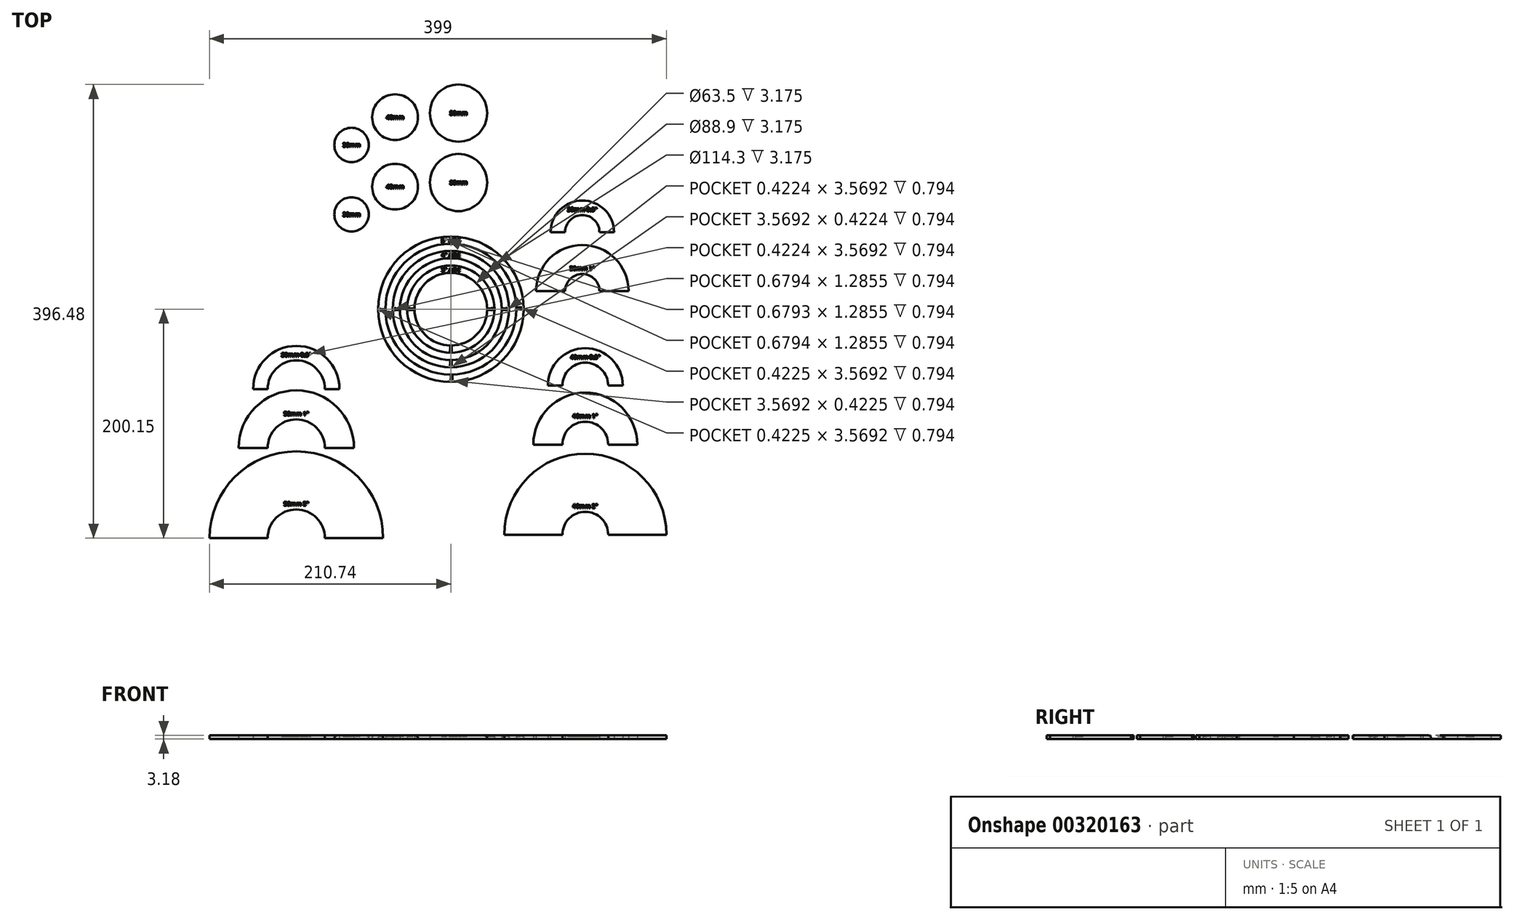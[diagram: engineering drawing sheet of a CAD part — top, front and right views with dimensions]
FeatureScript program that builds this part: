
annotation { "Feature Type Name" : "Feature", "Feature Type Description" : "" }
export const myFeature = defineFeature(function(context is Context, id is Id, definition is map)
    precondition{}
    {
        {
            var Q0;
            Q0=qCreatedBy(makeId("Top.planeOp"),FACE);
            var sketch = newSketch(context, id + "F0", { "sketchPlane" : qUnion([Q0])});
            skCircle(sketch, "E0", {"center": v(0, 0) * mm, "radius": 38.1 * mm});
            skCircle(sketch, "E1", {"center": v(0, 0) * mm, "radius": 31.75 * mm});
            skCircle(sketch, "E2", {"center": v(0, 0) * mm, "radius": 50.8 * mm});
            skCircle(sketch, "E3", {"center": v(0, 0) * mm, "radius": 44.45 * mm});
            skCircle(sketch, "E4", {"center": v(114.85, 67.2) * mm, "radius": 27.7 * mm});
            skCircle(sketch, "E5", {"center": v(114.85, 67.2) * mm, "radius": 15 * mm});
            skCircle(sketch, "E6", {"center": v(114.85, 67.2) * mm, "radius": 40.4 * mm});
            skCircle(sketch, "E7", {"center": v(117.46, -66.84) * mm, "radius": 32.7 * mm});
            skCircle(sketch, "E8", {"center": v(117.46, -66.84) * mm, "radius": 20 * mm});
            skCircle(sketch, "E9", {"center": v(117.46, -66.84) * mm, "radius": 45.4 * mm});
            skCircle(sketch, "E10", {"center": v(117.46, -66.84) * mm, "radius": 70.8 * mm});
            skLineSegment(sketch, "E11", {"start": v(74.45, 67.2) * mm, "end": v(87.15, 67.2) * mm});
            skLineSegment(sketch, "E12", {"start": v(87.15, 67.2) * mm, "end": v(99.85, 67.2) * mm});
            skLineSegment(sketch, "E13", {"start": v(99.85, 67.2) * mm, "end": v(114.85, 67.2) * mm});
            skLineSegment(sketch, "E14", {"start": v(129.85, 67.2) * mm, "end": v(114.85, 67.2) * mm});
            skLineSegment(sketch, "E15", {"start": v(129.85, 67.2) * mm, "end": v(142.55, 67.2) * mm});
            skLineSegment(sketch, "E16", {"start": v(142.55, 67.2) * mm, "end": v(155.25, 67.2) * mm});
            skLineSegment(sketch, "E17", {"start": v(117.46, -66.84) * mm, "end": v(97.46, -66.84) * mm});
            skLineSegment(sketch, "E18", {"start": v(97.46, -66.84) * mm, "end": v(84.76, -66.84) * mm});
            skLineSegment(sketch, "E19", {"start": v(84.76, -66.84) * mm, "end": v(72.06, -66.84) * mm});
            skLineSegment(sketch, "E20", {"start": v(72.06, -66.84) * mm, "end": v(46.66, -66.84) * mm});
            skLineSegment(sketch, "E21", {"start": v(117.46, -66.84) * mm, "end": v(137.46, -66.84) * mm});
            skLineSegment(sketch, "E22", {"start": v(137.46, -66.84) * mm, "end": v(150.16, -66.84) * mm});
            skLineSegment(sketch, "E23", {"start": v(150.16, -66.84) * mm, "end": v(162.86, -66.84) * mm});
            skLineSegment(sketch, "E24", {"start": v(162.86, -66.84) * mm, "end": v(188.26, -66.84) * mm});
            skCircle(sketch, "E25", {"center": v(-134.94, -69.85) * mm, "radius": 37.7 * mm});
            skCircle(sketch, "E26", {"center": v(-134.94, -69.85) * mm, "radius": 25 * mm});
            skCircle(sketch, "E27", {"center": v(-134.94, -69.85) * mm, "radius": 50.4 * mm});
            skCircle(sketch, "E28", {"center": v(-134.94, -69.85) * mm, "radius": 75.8 * mm});
            skLineSegment(sketch, "E29", {"start": v(-134.94, -69.85) * mm, "end": v(-159.94, -69.85) * mm});
            skLineSegment(sketch, "E30", {"start": v(-159.94, -69.85) * mm, "end": v(-172.64, -69.85) * mm});
            skLineSegment(sketch, "E31", {"start": v(-172.64, -69.85) * mm, "end": v(-185.34, -69.85) * mm});
            skLineSegment(sketch, "E32", {"start": v(-185.34, -69.85) * mm, "end": v(-210.74, -69.85) * mm});
            skLineSegment(sketch, "E33", {"start": v(-134.94, -69.85) * mm, "end": v(-109.94, -69.85) * mm});
            skLineSegment(sketch, "E34", {"start": v(-109.94, -69.85) * mm, "end": v(-97.24, -69.85) * mm});
            skLineSegment(sketch, "E35", {"start": v(-97.24, -69.85) * mm, "end": v(-84.54, -69.85) * mm});
            skLineSegment(sketch, "E36", {"start": v(-84.54, -69.85) * mm, "end": v(-59.14, -69.85) * mm});
            skCircle(sketch, "E37", {"center": v(0, 0) * mm, "radius": 57.15 * mm});
            skCircle(sketch, "E38", {"center": v(0, 0) * mm, "radius": 63.5 * mm});
            skCircle(sketch, "E39", {"center": v(-86.71, 82.78) * mm, "radius": 15 * mm});
            skCircle(sketch, "E40", {"center": v(-48.67, 107.05) * mm, "radius": 20 * mm});
            skCircle(sketch, "E41", {"center": v(6.75, 110.62) * mm, "radius": 25 * mm});
            skSolve(sketch);
        }
        {
            var Q0;
            Q0=makeQuery(id+"F0.imprint","IMPRINT",FACE,{"disambiguationData":[TD([[makeQuery(id+"F0.imprint","IMPRINT",EDGE,{"derivedFrom":sQuery(id+"F0.wireOp",EDGE,"E0")}),1.0]])]});
            var Q1;
            Q1=makeQuery(id+"F0.imprint","IMPRINT",FACE,{"disambiguationData":[TD([[makeQuery(id+"F0.imprint","IMPRINT",EDGE,{"derivedFrom":sQuery(id+"F0.wireOp",EDGE,"E2")}),1.0]])]});
            var Q2;
            {var subQ0=sQuery(id+"F0.wireOp",EDGE,"E12");Q2=makeQuery(id+"F0.imprint","IMPRINT",FACE,{"disambiguationData":[TD([[makeQuery(id+"F0.imprint","IMPRINT",EDGE,{"derivedFrom":subQ0}),1.0]])]});}
            var Q3;
            {var subQ0=sQuery(id+"F0.wireOp",EDGE,"E18");Q3=makeQuery(id+"F0.imprint","IMPRINT",FACE,{"disambiguationData":[TD([[makeQuery(id+"F0.imprint","IMPRINT",EDGE,{"derivedFrom":subQ0}),-1.0]])]});}
            var Q4;
            {var subQ0=sQuery(id+"F0.wireOp",EDGE,"E30");Q4=makeQuery(id+"F0.imprint","IMPRINT",FACE,{"disambiguationData":[TD([[makeQuery(id+"F0.imprint","IMPRINT",EDGE,{"derivedFrom":subQ0}),-1.0]])]});}
            var Q5;
            Q5=makeQuery(id+"F0.imprint","IMPRINT",FACE,{"disambiguationData":[TD([[makeQuery(id+"F0.imprint","IMPRINT",EDGE,{"derivedFrom":sQuery(id+"F0.wireOp",EDGE,"E37")}),-1.0]])]});
            var Q6;
            Q6=makeQuery(id+"F0.imprint","IMPRINT",FACE,{"disambiguationData":[TD([[makeQuery(id+"F0.imprint","IMPRINT",EDGE,{"derivedFrom":sQuery(id+"F0.wireOp",EDGE,"E41")}),1.0]])]});
            var Q7;
            Q7=makeQuery(id+"F0.imprint","IMPRINT",FACE,{"disambiguationData":[TD([[makeQuery(id+"F0.imprint","IMPRINT",EDGE,{"derivedFrom":sQuery(id+"F0.wireOp",EDGE,"E40")}),1.0]])]});
            var Q8;
            Q8=makeQuery(id+"F0.imprint","IMPRINT",FACE,{"disambiguationData":[TD([[makeQuery(id+"F0.imprint","IMPRINT",EDGE,{"derivedFrom":sQuery(id+"F0.wireOp",EDGE,"E39")}),1.0]])]});
            extrude(context, id + "F1", {"entities" : qUnion([Q0, Q1, Q2, Q3, Q4, Q5, Q6, Q7, Q8]), "depth" : 3.17 * mm});
        }
        {
            var Q0;
            {var subQ0=sQuery(id+"F0.wireOp",EDGE,"E30");Q0=makeQuery(id+"F0.imprint","IMPRINT",FACE,{"disambiguationData":[TD([[makeQuery(id+"F0.imprint","IMPRINT",EDGE,{"derivedFrom":subQ0}),-1.0]])]});}
            var Q1;
            {var subQ0=sQuery(id+"F0.wireOp",EDGE,"E31");Q1=makeQuery(id+"F0.imprint","IMPRINT",FACE,{"disambiguationData":[TD([[makeQuery(id+"F0.imprint","IMPRINT",EDGE,{"derivedFrom":subQ0}),-1.0]])]});}
            var Q2;
            {var subQ0=sQuery(id+"F0.wireOp",EDGE,"E18");Q2=makeQuery(id+"F0.imprint","IMPRINT",FACE,{"disambiguationData":[TD([[makeQuery(id+"F0.imprint","IMPRINT",EDGE,{"derivedFrom":subQ0}),-1.0]])]});}
            var Q3;
            {var subQ0=sQuery(id+"F0.wireOp",EDGE,"E19");Q3=makeQuery(id+"F0.imprint","IMPRINT",FACE,{"disambiguationData":[TD([[makeQuery(id+"F0.imprint","IMPRINT",EDGE,{"derivedFrom":subQ0}),-1.0]])]});}
            var Q4;
            {var subQ0=sQuery(id+"F0.wireOp",EDGE,"E12");Q4=makeQuery(id+"F0.imprint","IMPRINT",FACE,{"disambiguationData":[TD([[makeQuery(id+"F0.imprint","IMPRINT",EDGE,{"derivedFrom":subQ0}),1.0]])]});}
            var Q5;
            {var subQ0=sQuery(id+"F0.wireOp",EDGE,"E11");Q5=makeQuery(id+"F0.imprint","IMPRINT",FACE,{"disambiguationData":[TD([[makeQuery(id+"F0.imprint","IMPRINT",EDGE,{"derivedFrom":subQ0}),1.0]])]});}
            extrude(context, id + "F2", {"entities" : qUnion([Q0, Q1, Q2, Q3, Q4, Q5]), "depth" : 3.17 * mm});
        }
        {
            var Q0;
            {var subQ0=sQuery(id+"F0.wireOp",EDGE,"E18");Q0=makeQuery(id+"F0.imprint","IMPRINT",FACE,{"disambiguationData":[TD([[makeQuery(id+"F0.imprint","IMPRINT",EDGE,{"derivedFrom":subQ0}),-1.0]])]});}
            var Q1;
            {var subQ0=sQuery(id+"F0.wireOp",EDGE,"E19");Q1=makeQuery(id+"F0.imprint","IMPRINT",FACE,{"disambiguationData":[TD([[makeQuery(id+"F0.imprint","IMPRINT",EDGE,{"derivedFrom":subQ0}),-1.0]])]});}
            var Q2;
            {var subQ0=sQuery(id+"F0.wireOp",EDGE,"E20");Q2=makeQuery(id+"F0.imprint","IMPRINT",FACE,{"disambiguationData":[TD([[makeQuery(id+"F0.imprint","IMPRINT",EDGE,{"derivedFrom":subQ0}),-1.0]])]});}
            var Q3;
            {var subQ0=sQuery(id+"F0.wireOp",EDGE,"E30");Q3=makeQuery(id+"F0.imprint","IMPRINT",FACE,{"disambiguationData":[TD([[makeQuery(id+"F0.imprint","IMPRINT",EDGE,{"derivedFrom":subQ0}),-1.0]])]});}
            var Q4;
            {var subQ0=sQuery(id+"F0.wireOp",EDGE,"E31");Q4=makeQuery(id+"F0.imprint","IMPRINT",FACE,{"disambiguationData":[TD([[makeQuery(id+"F0.imprint","IMPRINT",EDGE,{"derivedFrom":subQ0}),-1.0]])]});}
            var Q5;
            {var subQ0=sQuery(id+"F0.wireOp",EDGE,"E32");Q5=makeQuery(id+"F0.imprint","IMPRINT",FACE,{"disambiguationData":[TD([[makeQuery(id+"F0.imprint","IMPRINT",EDGE,{"derivedFrom":subQ0}),-1.0]])]});}
            extrude(context, id + "F3", {"entities" : qUnion([Q0, Q1, Q2, Q3, Q4, Q5]), "depth" : 3.17 * mm});
        }
        {
            var Q0;
            Q0=makeQuery(id+"F2.opExtrude","SWEPT_BODY",BODY,{"disambiguationData":[OSD([sQuery(id+"F0.wireOp",EDGE,"E8"),sQuery(id+"F0.wireOp",EDGE,"E9"),sQuery(id+"F0.wireOp",EDGE,"E18"),sQuery(id+"F0.wireOp",EDGE,"E19"),sQuery(id+"F0.wireOp",EDGE,"E22"),sQuery(id+"F0.wireOp",EDGE,"E23")])]});
            var Q1;
            Q1=makeQuery(id+"F2.opExtrude","SWEPT_BODY",BODY,{"disambiguationData":[OSD([sQuery(id+"F0.wireOp",EDGE,"E26"),sQuery(id+"F0.wireOp",EDGE,"E27"),sQuery(id+"F0.wireOp",EDGE,"E30"),sQuery(id+"F0.wireOp",EDGE,"E31"),sQuery(id+"F0.wireOp",EDGE,"E34"),sQuery(id+"F0.wireOp",EDGE,"E35")])]});
            var Q2;
            Q2=makeQuery(id+"F2.opExtrude","SWEPT_BODY",BODY,{"disambiguationData":[OSD([sQuery(id+"F0.wireOp",EDGE,"E5"),sQuery(id+"F0.wireOp",EDGE,"E6"),sQuery(id+"F0.wireOp",EDGE,"E11"),sQuery(id+"F0.wireOp",EDGE,"E12"),sQuery(id+"F0.wireOp",EDGE,"E15"),sQuery(id+"F0.wireOp",EDGE,"E16")])]});
            transform(context, id + "F4", {"entities" : qUnion([Q0, Q1, Q2]), "transformType" : TransformType.TRANSLATION_3D, "dx" : 0 * mm, "dy" : -51.56 * mm, "dz" : 0 * mm, "makeCopy" : false});
        }
        {
            var Q0;
            Q0=makeQuery(id+"F3.opExtrude","SWEPT_BODY",BODY,{"disambiguationData":[OSD([sQuery(id+"F0.wireOp",EDGE,"E8"),sQuery(id+"F0.wireOp",EDGE,"E10"),sQuery(id+"F0.wireOp",EDGE,"E18"),sQuery(id+"F0.wireOp",EDGE,"E19"),sQuery(id+"F0.wireOp",EDGE,"E20"),sQuery(id+"F0.wireOp",EDGE,"E22"),sQuery(id+"F0.wireOp",EDGE,"E23"),sQuery(id+"F0.wireOp",EDGE,"E24")])]});
            var Q1;
            Q1=makeQuery(id+"F3.opExtrude","SWEPT_BODY",BODY,{"disambiguationData":[OSD([sQuery(id+"F0.wireOp",EDGE,"E26"),sQuery(id+"F0.wireOp",EDGE,"E28"),sQuery(id+"F0.wireOp",EDGE,"E30"),sQuery(id+"F0.wireOp",EDGE,"E31"),sQuery(id+"F0.wireOp",EDGE,"E32"),sQuery(id+"F0.wireOp",EDGE,"E34"),sQuery(id+"F0.wireOp",EDGE,"E35"),sQuery(id+"F0.wireOp",EDGE,"E36")])]});
            transform(context, id + "F5", {"entities" : qUnion([Q0, Q1]), "transformType" : TransformType.TRANSLATION_3D, "dx" : 0 * mm, "dy" : -130.3 * mm, "dz" : 0 * mm, "makeCopy" : false});
        }
        {
            var Q0;
            Q0=makeQuery(id+"F1.opExtrude","CAP_FACE",FACE,{"disambiguationData":[OSD([sQuery(id+"F0.wireOp",EDGE,"E2"),sQuery(id+"F0.wireOp",EDGE,"E3")])],"isStart":false});
            var sketch = newSketch(context, id + "F6", { "sketchPlane" : qUnion([Q0])});
            skText(sketch, "E42", { "text": "4\" AOE", "fontName": "OpenSans-Bold.ttf"});
            skText(sketch, "E43", { "text": "3\" AOE", "fontName": "OpenSans-Bold.ttf"});
            skText(sketch, "E44", { "text": "50mm 0.5\"", "fontName": "OpenSans-Bold.ttf"});
            skText(sketch, "E45", { "text": "50mm 1\"", "fontName": "OpenSans-Bold.ttf"});
            skText(sketch, "E46", { "text": "50mm 2\"", "fontName": "OpenSans-Bold.ttf"});
            skText(sketch, "E47", { "text": "30mm 0.5\"", "fontName": "OpenSans-Bold.ttf"});
            skArc(sketch, "E48.0.0", {"start": v(-159.94, -200.15) * mm, "mid": v(-134.94, -175.15) * mm, "end": v(-109.94, -200.15) * mm, "construction": true});
            skLineSegment(sketch, "E48.0.1", {"start": v(-109.94, -200.15) * mm, "end": v(-59.14, -200.15) * mm, "construction": true});
            skArc(sketch, "E48.0.2", {"start": v(-59.14, -200.15) * mm, "mid": v(-134.94, -124.35) * mm, "end": v(-210.74, -200.15) * mm, "construction": true});
            skLineSegment(sketch, "E48.0.3", {"start": v(-210.74, -200.15) * mm, "end": v(-159.94, -200.15) * mm, "construction": true});
            skArc(sketch, "E49.0.0", {"start": v(-159.94, -121.41) * mm, "mid": v(-134.94, -96.41) * mm, "end": v(-109.94, -121.41) * mm, "construction": true});
            skLineSegment(sketch, "E49.0.1", {"start": v(-109.94, -121.41) * mm, "end": v(-84.54, -121.41) * mm, "construction": true});
            skArc(sketch, "E49.0.2", {"start": v(-84.54, -121.41) * mm, "mid": v(-134.94, -71.01) * mm, "end": v(-185.34, -121.41) * mm, "construction": true});
            skLineSegment(sketch, "E49.0.3", {"start": v(-185.34, -121.41) * mm, "end": v(-159.94, -121.41) * mm, "construction": true});
            skArc(sketch, "E50.0.0", {"start": v(-159.94, -69.85) * mm, "mid": v(-134.94, -44.85) * mm, "end": v(-109.94, -69.85) * mm, "construction": true});
            skLineSegment(sketch, "E50.0.1", {"start": v(-109.94, -69.85) * mm, "end": v(-97.24, -69.85) * mm, "construction": true});
            skArc(sketch, "E50.0.2", {"start": v(-97.24, -69.85) * mm, "mid": v(-134.94, -32.15) * mm, "end": v(-172.64, -69.85) * mm, "construction": true});
            skLineSegment(sketch, "E50.0.3", {"start": v(-172.64, -69.85) * mm, "end": v(-159.94, -69.85) * mm, "construction": true});
            skArc(sketch, "E51.0.0", {"start": v(97.46, -197.14) * mm, "mid": v(117.46, -177.14) * mm, "end": v(137.46, -197.14) * mm, "construction": true});
            skLineSegment(sketch, "E51.0.1", {"start": v(137.46, -197.14) * mm, "end": v(188.26, -197.14) * mm, "construction": true});
            skArc(sketch, "E51.0.2", {"start": v(188.26, -197.14) * mm, "mid": v(117.46, -126.34) * mm, "end": v(46.66, -197.14) * mm, "construction": true});
            skLineSegment(sketch, "E51.0.3", {"start": v(46.66, -197.14) * mm, "end": v(97.46, -197.14) * mm, "construction": true});
            skArc(sketch, "E52.0.0", {"start": v(97.46, -118.4) * mm, "mid": v(117.46, -98.4) * mm, "end": v(137.46, -118.4) * mm, "construction": true});
            skLineSegment(sketch, "E52.0.1", {"start": v(137.46, -118.4) * mm, "end": v(162.86, -118.4) * mm, "construction": true});
            skArc(sketch, "E52.0.2", {"start": v(162.86, -118.4) * mm, "mid": v(117.46, -73) * mm, "end": v(72.06, -118.4) * mm, "construction": true});
            skLineSegment(sketch, "E52.0.3", {"start": v(72.06, -118.4) * mm, "end": v(97.46, -118.4) * mm, "construction": true});
            skArc(sketch, "E53.0.0", {"start": v(97.46, -66.84) * mm, "mid": v(117.46, -46.84) * mm, "end": v(137.46, -66.84) * mm, "construction": true});
            skLineSegment(sketch, "E53.0.1", {"start": v(137.46, -66.84) * mm, "end": v(150.16, -66.84) * mm, "construction": true});
            skArc(sketch, "E53.0.2", {"start": v(150.16, -66.84) * mm, "mid": v(117.46, -34.14) * mm, "end": v(84.76, -66.84) * mm, "construction": true});
            skLineSegment(sketch, "E53.0.3", {"start": v(84.76, -66.84) * mm, "end": v(97.46, -66.84) * mm, "construction": true});
            skArc(sketch, "E54.0.0", {"start": v(99.85, 15.64) * mm, "mid": v(114.85, 30.64) * mm, "end": v(129.85, 15.64) * mm, "construction": true});
            skLineSegment(sketch, "E54.0.1", {"start": v(129.85, 15.64) * mm, "end": v(155.25, 15.64) * mm, "construction": true});
            skArc(sketch, "E54.0.2", {"start": v(155.25, 15.64) * mm, "mid": v(114.85, 56.04) * mm, "end": v(74.45, 15.64) * mm, "construction": true});
            skLineSegment(sketch, "E54.0.3", {"start": v(74.45, 15.64) * mm, "end": v(99.85, 15.64) * mm, "construction": true});
            skArc(sketch, "E55.0.0", {"start": v(99.85, 67.2) * mm, "mid": v(114.85, 82.2) * mm, "end": v(129.85, 67.2) * mm, "construction": true});
            skLineSegment(sketch, "E55.0.1", {"start": v(129.85, 67.2) * mm, "end": v(142.55, 67.2) * mm, "construction": true});
            skArc(sketch, "E55.0.2", {"start": v(142.55, 67.2) * mm, "mid": v(114.85, 94.9) * mm, "end": v(87.15, 67.2) * mm, "construction": true});
            skLineSegment(sketch, "E55.0.3", {"start": v(87.15, 67.2) * mm, "end": v(99.85, 67.2) * mm, "construction": true});
            skPoint(sketch, "E56", {"position": v(-134.94, -44.85) * mm});
            skPoint(sketch, "E57", {"position": v(-134.94, -96.41) * mm});
            skPoint(sketch, "E58", {"position": v(-134.94, -175.15) * mm});
            skPoint(sketch, "E59", {"position": v(114.85, 82.2) * mm});
            skText(sketch, "E60", { "text": "30mm 1\"", "fontName": "OpenSans-Bold.ttf"});
            skText(sketch, "E61", { "text": "40mm 0.5\"", "fontName": "OpenSans-Bold.ttf"});
            skText(sketch, "E62", { "text": "40mm 1\"", "fontName": "OpenSans-Bold.ttf"});
            skText(sketch, "E63", { "text": "40mm 2\"", "fontName": "OpenSans-Bold.ttf"});
            skPoint(sketch, "E64", {"position": v(114.85, 30.64) * mm});
            skPoint(sketch, "E65", {"position": v(117.46, -46.84) * mm});
            skPoint(sketch, "E66", {"position": v(117.46, -98.4) * mm});
            skPoint(sketch, "E67", {"position": v(117.46, -177.14) * mm});
            skLineSegment(sketch, "E68", {"start": v(0, 50.8) * mm, "end": v(0, 0) * mm, "construction": true});
            skLineSegment(sketch, "E69", {"start": v(0, 0) * mm, "end": v(50.8, 0) * mm, "construction": true});
            skLineSegment(sketch, "E70", {"start": v(50.23, 0) * mm, "end": v(50.23, -1.78) * mm});
            skLineSegment(sketch, "E71", {"start": v(50.23, -1.78) * mm, "end": v(49.81, -1.78) * mm});
            skLineSegment(sketch, "E72", {"start": v(49.81, -1.78) * mm, "end": v(49.81, 0) * mm});
            skLineSegment(sketch, "E73", {"start": v(49.81, 0) * mm, "end": v(49.81, 1.78) * mm});
            skLineSegment(sketch, "E74", {"start": v(49.81, 1.78) * mm, "end": v(50.23, 1.78) * mm});
            skLineSegment(sketch, "E75", {"start": v(50.23, 1.78) * mm, "end": v(50.23, 0) * mm});
            skLineSegment(sketch, "E76", {"start": v(49.5, 0) * mm, "end": v(47.76, -1.34) * mm});
            skLineSegment(sketch, "E77", {"start": v(47.76, -1.34) * mm, "end": v(47.76, 0) * mm});
            skLineSegment(sketch, "E78", {"start": v(47.76, 0) * mm, "end": v(47.76, 1.34) * mm});
            skLineSegment(sketch, "E79", {"start": v(47.76, 1.34) * mm, "end": v(49.5, 0) * mm});
            skLineSegment(sketch, "E80", {"start": v(47.76, -0.67) * mm, "end": v(45.62, -0.67) * mm});
            skLineSegment(sketch, "E81", {"start": v(45.62, -0.67) * mm, "end": v(45.62, 0.67) * mm});
            skLineSegment(sketch, "E82", {"start": v(45.62, 0.67) * mm, "end": v(47.76, 0.67) * mm});
            skPoint(sketch, "E82.endSnap0", {"position": v(47.76, 0.67) * mm});
            skLineSegment(sketch, "E83", {"start": v(37.54, 0) * mm, "end": v(37.55, -1.78) * mm});
            skLineSegment(sketch, "E84", {"start": v(37.55, -1.78) * mm, "end": v(37.12, -1.79) * mm});
            skLineSegment(sketch, "E85", {"start": v(37.12, -1.79) * mm, "end": v(37.12, 0) * mm});
            skLineSegment(sketch, "E86", {"start": v(37.12, 0) * mm, "end": v(37.1, 1.79) * mm});
            skLineSegment(sketch, "E87", {"start": v(37.1, 1.79) * mm, "end": v(37.53, 1.78) * mm});
            skLineSegment(sketch, "E88", {"start": v(37.53, 1.78) * mm, "end": v(37.54, 0) * mm});
            skLineSegment(sketch, "E89", {"start": v(36.8, 0) * mm, "end": v(35.07, -1.34) * mm});
            skLineSegment(sketch, "E90", {"start": v(35.07, -1.34) * mm, "end": v(35.07, 0) * mm});
            skLineSegment(sketch, "E91", {"start": v(35.07, 0) * mm, "end": v(35.06, 1.34) * mm});
            skLineSegment(sketch, "E92", {"start": v(35.06, 1.34) * mm, "end": v(36.8, 0) * mm});
            skLineSegment(sketch, "E93", {"start": v(35.07, -0.67) * mm, "end": v(32.93, -0.68) * mm});
            skLineSegment(sketch, "E94", {"start": v(32.93, -0.68) * mm, "end": v(32.92, 0.66) * mm});
            skLineSegment(sketch, "E95", {"start": v(32.92, 0.66) * mm, "end": v(35.06, 0.67) * mm});
            skPoint(sketch, "E95.endSnap0", {"position": v(35.06, 0.67) * mm});
            skLineSegment(sketch, "E96.1.0", {"start": v(-0.68, -32.93) * mm, "end": v(0.66, -32.92) * mm});
            skLineSegment(sketch, "E96.1.1", {"start": v(0, -47.76) * mm, "end": v(1.34, -47.76) * mm});
            skLineSegment(sketch, "E96.1.2", {"start": v(-1.78, -49.81) * mm, "end": v(0, -49.81) * mm});
            skLineSegment(sketch, "E96.1.3", {"start": v(-1.78, -37.55) * mm, "end": v(-1.79, -37.12) * mm});
            skLineSegment(sketch, "E96.1.4", {"start": v(-1.34, -47.76) * mm, "end": v(0, -47.76) * mm});
            skLineSegment(sketch, "E96.1.5", {"start": v(-0.67, -35.07) * mm, "end": v(-0.68, -32.93) * mm});
            skLineSegment(sketch, "E96.1.6", {"start": v(1.79, -37.1) * mm, "end": v(1.78, -37.53) * mm});
            skLineSegment(sketch, "E96.1.7", {"start": v(1.78, -37.53) * mm, "end": v(0, -37.54) * mm});
            skLineSegment(sketch, "E96.1.8", {"start": v(-0.67, -45.62) * mm, "end": v(0.67, -45.62) * mm});
            skLineSegment(sketch, "E96.1.9", {"start": v(0, -35.07) * mm, "end": v(1.34, -35.06) * mm});
            skLineSegment(sketch, "E96.1.10", {"start": v(-1.79, -37.12) * mm, "end": v(0, -37.12) * mm});
            skLineSegment(sketch, "E96.1.11", {"start": v(-1.78, -50.23) * mm, "end": v(-1.78, -49.81) * mm});
            skLineSegment(sketch, "E96.1.12", {"start": v(-0.67, -47.76) * mm, "end": v(-0.67, -45.62) * mm});
            skLineSegment(sketch, "E96.1.13", {"start": v(1.78, -50.23) * mm, "end": v(0, -50.23) * mm});
            skPoint(sketch, "E96.1.14", {"position": v(0.67, -47.76) * mm});
            skLineSegment(sketch, "E96.1.15", {"start": v(0, -49.81) * mm, "end": v(1.78, -49.81) * mm});
            skLineSegment(sketch, "E96.1.16", {"start": v(0, -36.8) * mm, "end": v(-1.34, -35.07) * mm});
            skLineSegment(sketch, "E96.1.17", {"start": v(0.67, -45.62) * mm, "end": v(0.67, -47.76) * mm});
            skPoint(sketch, "E96.1.18", {"position": v(0.67, -35.06) * mm});
            skLineSegment(sketch, "E96.1.19", {"start": v(1.34, -47.76) * mm, "end": v(0, -49.5) * mm});
            skLineSegment(sketch, "E96.1.20", {"start": v(0, -37.12) * mm, "end": v(1.79, -37.1) * mm});
            skLineSegment(sketch, "E96.1.21", {"start": v(0.66, -32.92) * mm, "end": v(0.67, -35.06) * mm});
            skLineSegment(sketch, "E96.1.22", {"start": v(1.34, -35.06) * mm, "end": v(0, -36.8) * mm});
            skLineSegment(sketch, "E96.1.23", {"start": v(0, -49.5) * mm, "end": v(-1.34, -47.76) * mm});
            skLineSegment(sketch, "E96.1.24", {"start": v(1.78, -49.81) * mm, "end": v(1.78, -50.23) * mm});
            skLineSegment(sketch, "E96.1.25", {"start": v(-1.34, -35.07) * mm, "end": v(0, -35.07) * mm});
            skLineSegment(sketch, "E96.1.26", {"start": v(0, -37.54) * mm, "end": v(-1.78, -37.55) * mm});
            skLineSegment(sketch, "E96.1.27", {"start": v(0, -50.23) * mm, "end": v(-1.78, -50.23) * mm});
            skLineSegment(sketch, "E96.2.0", {"start": v(-32.93, 0.68) * mm, "end": v(-32.92, -0.66) * mm});
            skLineSegment(sketch, "E96.2.1", {"start": v(-47.76, 0) * mm, "end": v(-47.76, -1.34) * mm});
            skLineSegment(sketch, "E96.2.2", {"start": v(-49.81, 1.78) * mm, "end": v(-49.81, 0) * mm});
            skLineSegment(sketch, "E96.2.3", {"start": v(-37.55, 1.78) * mm, "end": v(-37.12, 1.79) * mm});
            skLineSegment(sketch, "E96.2.4", {"start": v(-47.76, 1.34) * mm, "end": v(-47.76, 0) * mm});
            skLineSegment(sketch, "E96.2.5", {"start": v(-35.07, 0.67) * mm, "end": v(-32.93, 0.68) * mm});
            skLineSegment(sketch, "E96.2.6", {"start": v(-37.1, -1.79) * mm, "end": v(-37.53, -1.78) * mm});
            skLineSegment(sketch, "E96.2.7", {"start": v(-37.53, -1.78) * mm, "end": v(-37.54, 0) * mm});
            skLineSegment(sketch, "E96.2.8", {"start": v(-45.62, 0.67) * mm, "end": v(-45.62, -0.67) * mm});
            skLineSegment(sketch, "E96.2.9", {"start": v(-35.07, 0) * mm, "end": v(-35.06, -1.34) * mm});
            skLineSegment(sketch, "E96.2.10", {"start": v(-37.12, 1.79) * mm, "end": v(-37.12, 0) * mm});
            skLineSegment(sketch, "E96.2.11", {"start": v(-50.23, 1.78) * mm, "end": v(-49.81, 1.78) * mm});
            skLineSegment(sketch, "E96.2.12", {"start": v(-47.76, 0.67) * mm, "end": v(-45.62, 0.67) * mm});
            skLineSegment(sketch, "E96.2.13", {"start": v(-50.23, -1.78) * mm, "end": v(-50.23, 0) * mm});
            skPoint(sketch, "E96.2.14", {"position": v(-47.76, -0.67) * mm});
            skLineSegment(sketch, "E96.2.15", {"start": v(-49.81, 0) * mm, "end": v(-49.81, -1.78) * mm});
            skLineSegment(sketch, "E96.2.16", {"start": v(-36.8, 0) * mm, "end": v(-35.07, 1.34) * mm});
            skLineSegment(sketch, "E96.2.17", {"start": v(-45.62, -0.67) * mm, "end": v(-47.76, -0.67) * mm});
            skPoint(sketch, "E96.2.18", {"position": v(-35.06, -0.67) * mm});
            skLineSegment(sketch, "E96.2.19", {"start": v(-47.76, -1.34) * mm, "end": v(-49.5, 0) * mm});
            skLineSegment(sketch, "E96.2.20", {"start": v(-37.12, 0) * mm, "end": v(-37.1, -1.79) * mm});
            skLineSegment(sketch, "E96.2.21", {"start": v(-32.92, -0.66) * mm, "end": v(-35.06, -0.67) * mm});
            skLineSegment(sketch, "E96.2.22", {"start": v(-35.06, -1.34) * mm, "end": v(-36.8, 0) * mm});
            skLineSegment(sketch, "E96.2.23", {"start": v(-49.5, 0) * mm, "end": v(-47.76, 1.34) * mm});
            skLineSegment(sketch, "E96.2.24", {"start": v(-49.81, -1.78) * mm, "end": v(-50.23, -1.78) * mm});
            skLineSegment(sketch, "E96.2.25", {"start": v(-35.07, 1.34) * mm, "end": v(-35.07, 0) * mm});
            skLineSegment(sketch, "E96.2.26", {"start": v(-37.54, 0) * mm, "end": v(-37.55, 1.78) * mm});
            skLineSegment(sketch, "E96.2.27", {"start": v(-50.23, 0) * mm, "end": v(-50.23, 1.78) * mm});
            skPoint(sketch, "E96.center", {"position": v(0, 0) * mm});
            skLineSegment(sketch, "E96.anchor1", {"start": v(0, 0) * mm, "end": v(32.93, -0.68) * mm, "construction": true});
            skLineSegment(sketch, "E96.anchor2", {"start": v(0, 0) * mm, "end": v(-32.93, 0.68) * mm, "construction": true});
            skText(sketch, "E97", { "text": "5\" AOE", "fontName": "OpenSans-Bold.ttf"});
            skLineSegment(sketch, "E98", {"start": v(0, 50.8) * mm, "end": v(0, 63.4) * mm, "construction": true});
            skLineSegment(sketch, "E99", {"start": v(62.9, 0.68) * mm, "end": v(62.9, -1.1) * mm});
            skLineSegment(sketch, "E100", {"start": v(62.9, -1.1) * mm, "end": v(62.48, -1.1) * mm});
            skLineSegment(sketch, "E101", {"start": v(62.48, -1.1) * mm, "end": v(62.48, 0.68) * mm});
            skLineSegment(sketch, "E102", {"start": v(62.48, 0.68) * mm, "end": v(62.48, 2.47) * mm});
            skLineSegment(sketch, "E103", {"start": v(62.48, 2.47) * mm, "end": v(62.9, 2.47) * mm});
            skLineSegment(sketch, "E104", {"start": v(62.9, 2.47) * mm, "end": v(62.9, 0.68) * mm});
            skLineSegment(sketch, "E105", {"start": v(62.18, 0.68) * mm, "end": v(60.43, -0.66) * mm});
            skLineSegment(sketch, "E106", {"start": v(60.43, -0.66) * mm, "end": v(60.43, 0.68) * mm});
            skLineSegment(sketch, "E107", {"start": v(60.43, 0.68) * mm, "end": v(60.43, 2.02) * mm});
            skLineSegment(sketch, "E108", {"start": v(60.43, 2.02) * mm, "end": v(62.18, 0.68) * mm});
            skLineSegment(sketch, "E109", {"start": v(60.43, 0.01) * mm, "end": v(58.29, 0.01) * mm});
            skLineSegment(sketch, "E110", {"start": v(58.29, 0.01) * mm, "end": v(58.29, 1.35) * mm});
            skLineSegment(sketch, "E111", {"start": v(58.29, 1.35) * mm, "end": v(60.43, 1.35) * mm});
            skPoint(sketch, "E111.endSnap0", {"position": v(60.43, 1.35) * mm});
            skPoint(sketch, "E112.1.0", {"position": v(1.35, -60.43) * mm});
            skLineSegment(sketch, "E112.1.1", {"start": v(1.35, -58.29) * mm, "end": v(1.35, -60.43) * mm});
            skLineSegment(sketch, "E112.1.2", {"start": v(0.01, -60.43) * mm, "end": v(0.01, -58.29) * mm});
            skLineSegment(sketch, "E112.1.3", {"start": v(0.01, -58.29) * mm, "end": v(1.35, -58.29) * mm});
            skLineSegment(sketch, "E112.1.4", {"start": v(-1.1, -62.48) * mm, "end": v(0.68, -62.48) * mm});
            skLineSegment(sketch, "E112.1.5", {"start": v(0.68, -62.18) * mm, "end": v(-0.66, -60.43) * mm});
            skLineSegment(sketch, "E112.1.6", {"start": v(-1.1, -62.9) * mm, "end": v(-1.1, -62.48) * mm});
            skLineSegment(sketch, "E112.1.7", {"start": v(2.47, -62.9) * mm, "end": v(0.68, -62.9) * mm});
            skLineSegment(sketch, "E112.1.8", {"start": v(-0.66, -60.43) * mm, "end": v(0.68, -60.43) * mm});
            skLineSegment(sketch, "E112.1.9", {"start": v(2.02, -60.43) * mm, "end": v(0.68, -62.18) * mm});
            skLineSegment(sketch, "E112.1.10", {"start": v(2.47, -62.48) * mm, "end": v(2.47, -62.9) * mm});
            skLineSegment(sketch, "E112.1.11", {"start": v(0.68, -60.43) * mm, "end": v(2.02, -60.43) * mm});
            skLineSegment(sketch, "E112.1.12", {"start": v(0.68, -62.9) * mm, "end": v(-1.1, -62.9) * mm});
            skLineSegment(sketch, "E112.1.13", {"start": v(0.68, -62.48) * mm, "end": v(2.47, -62.48) * mm});
            skPoint(sketch, "E112.2.0", {"position": v(-60.43, -1.35) * mm});
            skLineSegment(sketch, "E112.2.1", {"start": v(-58.29, -1.35) * mm, "end": v(-60.43, -1.35) * mm});
            skLineSegment(sketch, "E112.2.2", {"start": v(-60.43, -0.01) * mm, "end": v(-58.29, -0.01) * mm});
            skLineSegment(sketch, "E112.2.3", {"start": v(-58.29, -0.01) * mm, "end": v(-58.29, -1.35) * mm});
            skLineSegment(sketch, "E112.2.4", {"start": v(-62.48, 1.1) * mm, "end": v(-62.48, -0.68) * mm});
            skLineSegment(sketch, "E112.2.5", {"start": v(-62.18, -0.68) * mm, "end": v(-60.43, 0.66) * mm});
            skLineSegment(sketch, "E112.2.6", {"start": v(-62.9, 1.1) * mm, "end": v(-62.48, 1.1) * mm});
            skLineSegment(sketch, "E112.2.7", {"start": v(-62.9, -2.47) * mm, "end": v(-62.9, -0.68) * mm});
            skLineSegment(sketch, "E112.2.8", {"start": v(-60.43, 0.66) * mm, "end": v(-60.43, -0.68) * mm});
            skLineSegment(sketch, "E112.2.9", {"start": v(-60.43, -2.02) * mm, "end": v(-62.18, -0.68) * mm});
            skLineSegment(sketch, "E112.2.10", {"start": v(-62.48, -2.47) * mm, "end": v(-62.9, -2.47) * mm});
            skLineSegment(sketch, "E112.2.11", {"start": v(-60.43, -0.68) * mm, "end": v(-60.43, -2.02) * mm});
            skLineSegment(sketch, "E112.2.12", {"start": v(-62.9, -0.68) * mm, "end": v(-62.9, 1.1) * mm});
            skLineSegment(sketch, "E112.2.13", {"start": v(-62.48, -0.68) * mm, "end": v(-62.48, -2.47) * mm});
            skLineSegment(sketch, "E112.anchor1", {"start": v(0, 0) * mm, "end": v(58.29, 0.01) * mm, "construction": true});
            skLineSegment(sketch, "E112.anchor2", {"start": v(0, 0) * mm, "end": v(-58.29, -0.01) * mm, "construction": true});
            skText(sketch, "E113", { "text": "30mm", "fontName": "OpenSans-Bold.ttf"});
            skCircle(sketch, "E114.0.0", {"center": v(-86.71, 82.78) * mm, "radius": 15 * mm, "construction": true});
            skCircle(sketch, "E114.1.0", {"center": v(-48.67, 107.05) * mm, "radius": 20 * mm, "construction": true});
            skCircle(sketch, "E114.2.0", {"center": v(6.75, 110.62) * mm, "radius": 25 * mm, "construction": true});
            skText(sketch, "E115", { "text": "50mm\n", "fontName": "OpenSans-Bold.ttf"});
            skText(sketch, "E116", { "text": "40mm", "fontName": "OpenSans-Bold.ttf"});
            const initialGuessF6  = {"E42": [-0.00836, 0.0454, 1, 0, 0.00359], "E43": [-0.00836, 0.03252, 1, 0, 0.00359], "E44": [-0.14806, -0.04168, 1, 0, 0.00359], "E45": [-0.14592, -0.09324, 1, 0, 0.00359], "E46": [-0.14592, -0.17198, 1, 0, 0.00359], "E47": [0.10173, 0.08538, 1, 0, 0.00359], "E60": [0.10386, 0.03382, 1, 0, 0.00359], "E61": [0.10435, -0.04367, 1, 0, 0.00359], "E62": [0.10648, -0.09523, 1, 0, 0.00359], "E63": [0.10648, -0.17397, 1, 0, 0.00359], "E97": [-0.00836, 0.0581, 1, 0, 0.00359], "E113": [-0.09443, 0.08098, 1, 0, 0.00359], "E115": [-0.00096, 0.10883, 1, 0, 0.00359], "E116": [-0.05638, 0.10525, 1, 0, 0.00359]};
            skSetInitialGuess(sketch, initialGuessF6);
            skSolve(sketch);
        }
        {
            var Q0;
            Q0 = qSketchRegion(id + "F6", true);
            extrude(context, id + "F7", {"entities" : qUnion([Q0]), "operationType" : NewBodyOperationType.REMOVE, "oppositeDirection" : true, "depth" : 0.8 * mm});
        }
        {
            var Q0;
            Q0=makeQuery(id+"F1.opExtrude","SWEPT_BODY",BODY,{"disambiguationData":[OSD([sQuery(id+"F0.wireOp",EDGE,"E39")])]});
            var Q1;
            Q1=makeQuery(id+"F1.opExtrude","SWEPT_BODY",BODY,{"disambiguationData":[OSD([sQuery(id+"F0.wireOp",EDGE,"E40")])]});
            var Q2;
            Q2=makeQuery(id+"F1.opExtrude","SWEPT_BODY",BODY,{"disambiguationData":[OSD([sQuery(id+"F0.wireOp",EDGE,"E41")])]});
            transform(context, id + "F8", {"entities" : qUnion([Q0, Q1, Q2]), "transformType" : TransformType.TRANSLATION_3D, "dx" : 0 * mm, "dy" : 60.7 * mm, "dz" : 0 * mm, "makeCopy" : true});
        }
        {
            var Q0;
            Q0=makeQuery(id+"F1.opExtrude","CAP_EDGE",EDGE,{"disambiguationData":[OSD([sQuery(id+"F0.wireOp",EDGE,"E39")])],"isStart":false});
            var Q1;
            Q1=makeQuery(id+"F1.opExtrude","CAP_EDGE",EDGE,{"disambiguationData":[OSD([sQuery(id+"F0.wireOp",EDGE,"E40")])],"isStart":false});
            var Q2;
            Q2=makeQuery(id+"F1.opExtrude","CAP_EDGE",EDGE,{"disambiguationData":[OSD([sQuery(id+"F0.wireOp",EDGE,"E41")])],"isStart":false});
            fillet(context, id + "F9", {"entities" : qUnion([Q0, Q1, Q2]), "radius" : 2.54 * mm, "tangentPropagation" : true, "allowEdgeOverflow" : false});
        }
    });
